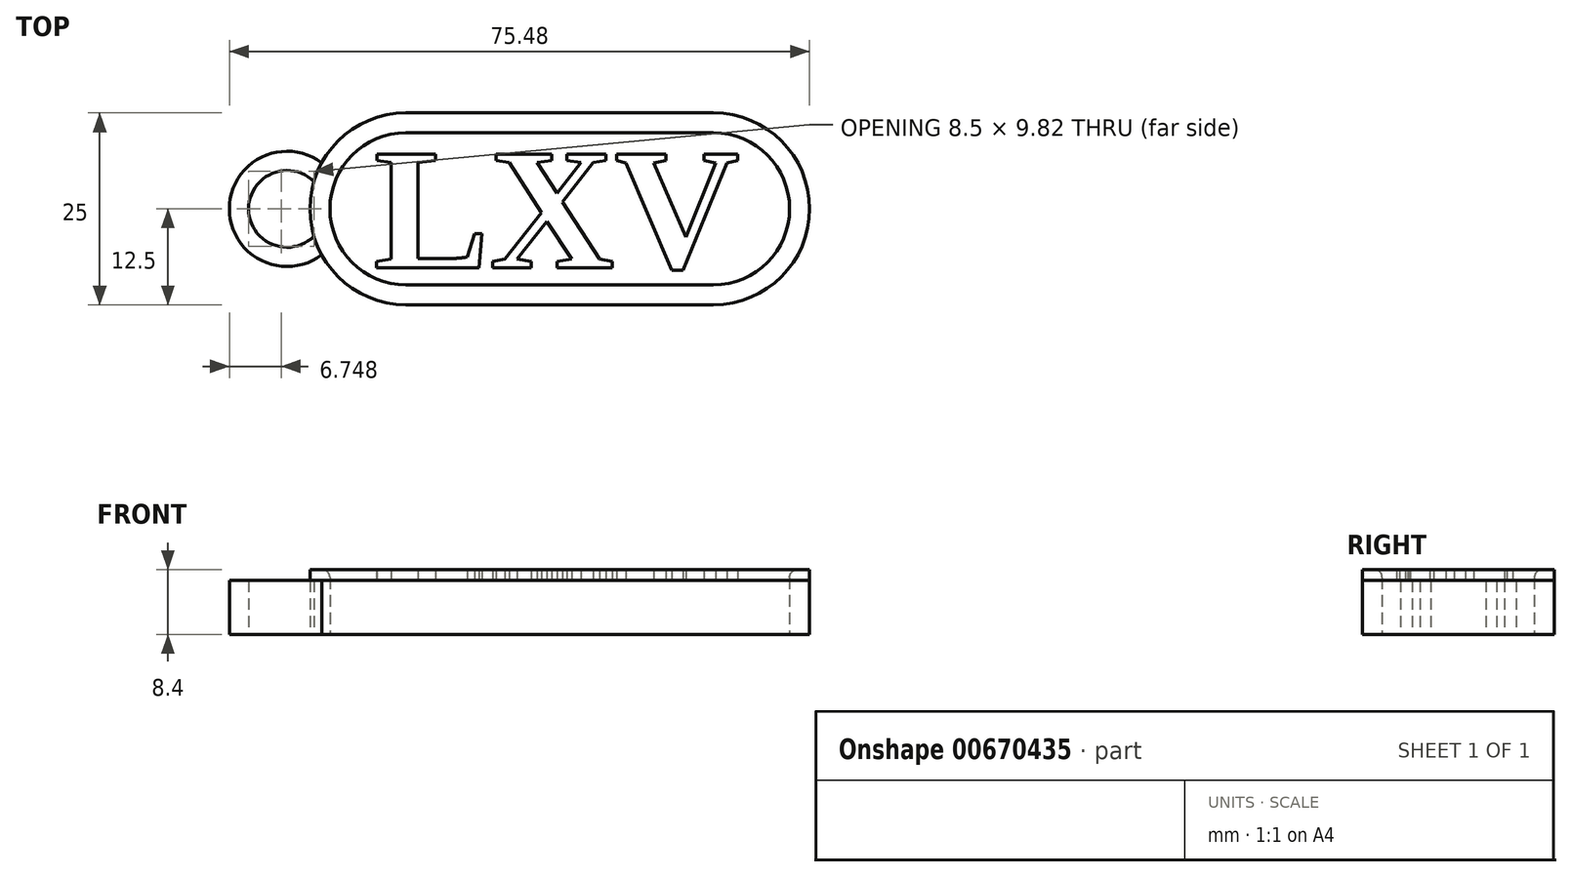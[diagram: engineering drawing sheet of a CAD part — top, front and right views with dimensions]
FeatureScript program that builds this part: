
annotation { "Feature Type Name" : "Feature", "Feature Type Description" : "" }
export const myFeature = defineFeature(function(context is Context, id is Id, definition is map)
    precondition{}
    {
        {
            var Q0;
            Q0=qCreatedBy(makeId("Top.planeOp"),FACE);
            var sketch = newSketch(context, id + "F0", { "sketchPlane" : qUnion([Q0])});
            skLineSegment(sketch, "E0.bottom", {"start": v(-20, 12.5) * mm, "end": v(20, 12.5) * mm});
            skLineSegment(sketch, "E0.top", {"start": v(-20, -12.5) * mm, "end": v(20, -12.5) * mm});
            skLineSegment(sketch, "E0.left", {"start": v(-20, 12.5) * mm, "end": v(-20, -12.5) * mm});
            skLineSegment(sketch, "E0.right", {"start": v(20, 12.5) * mm, "end": v(20, -12.5) * mm});
            skPoint(sketch, "E0.middle", {"position": v(0, 0) * mm});
            skArc(sketch, "E1", {"start": v(-20, 12.5) * mm, "mid": v(-32.5, 0) * mm, "end": v(-20, -12.5) * mm});
            skArc(sketch, "E2", {"start": v(20, 12.5) * mm, "mid": v(32.5, 0) * mm, "end": v(20, -12.5) * mm});
            skCircle(sketch, "E3", {"center": v(-35.48, 0) * mm, "radius": 5 * mm});
            skCircle(sketch, "E4", {"center": v(-35.48, 0) * mm, "radius": 7.5 * mm});
            skSolve(sketch);
        }
        {
            var Q0;
            {var subQ0=sQuery(id+"F0.wireOp",EDGE,"E0.left");Q0=makeQuery(id+"F0.imprint","IMPRINT",FACE,{"disambiguationData":[TD([[makeQuery(id+"F0.imprint","IMPRINT",EDGE,{"derivedFrom":subQ0}),-1.0]])]});}
            var Q1;
            Q1=makeQuery(id+"F0.imprint","IMPRINT",FACE,{"disambiguationData":[TD([[makeQuery(id+"F0.imprint","IMPRINT",EDGE,{"derivedFrom":sQuery(id+"F0.wireOp",EDGE,"E0.bottom")}),-1.0]])]});
            var Q2;
            Q2=makeQuery(id+"F0.imprint","IMPRINT",FACE,{"disambiguationData":[TD([[makeQuery(id+"F0.imprint","IMPRINT",EDGE,{"derivedFrom":sQuery(id+"F0.wireOp",EDGE,"E0.right")}),1.0]])]});
            var Q3;
            Q3=makeQuery(id+"F0.imprint","IMPRINT",FACE,{"disambiguationData":[TD([[makeQuery(id+"F0.imprint","IMPRINT",EDGE,{"derivedFrom":sQuery(id+"F0.wireOp",EDGE,"E4")}),-1.0]])]});
            var Q4;
            {var subQ0=sQuery(id+"F0.wireOp",EDGE,"E3");var subQ1=sQuery(id+"F0.wireOp",EDGE,"E1");var subQ2=makeQuery(id+"F0.imprint","INTERSECT",VERTEX,{"disambiguationData":[OD(0.0)],"derivedFrom":[subQ1,subQ0]});Q4=makeQuery(id+"F0.imprint","IMPRINT",FACE,{"disambiguationData":[TD([[makeQuery(id+"F0.imprint","IMPRINT",EDGE,{"disambiguationData":[TD([[subQ2,-1.0]])],"derivedFrom":subQ1}),1.0]])]});}
            extrude(context, id + "F1", {"entities" : qUnion([Q0, Q1, Q2, Q3, Q4]), "depth" : 5 * mm, "offsetDistance" : 25 * mm});
        }
        {
            var Q0;
            Q0=qCreatedBy(makeId("Top.planeOp"),FACE);
            var sketch = newSketch(context, id + "F2", { "sketchPlane" : qUnion([Q0])});
            skArc(sketch, "E5.0", {"start": v(-20, 9.9) * mm, "mid": v(-29.9, 0) * mm, "end": v(-20, -9.9) * mm});
            skLineSegment(sketch, "E5.1", {"start": v(-20, 9.9) * mm, "end": v(20, 9.9) * mm});
            skArc(sketch, "E5.2", {"start": v(20, 9.9) * mm, "mid": v(29.9, 0) * mm, "end": v(20, -9.9) * mm});
            skLineSegment(sketch, "E5.3", {"start": v(-20, -9.9) * mm, "end": v(20, -9.9) * mm});
            skLineSegment(sketch, "E6.0", {"start": v(-20, 12.5) * mm, "end": v(20, 12.5) * mm});
            skArc(sketch, "E6.1", {"start": v(-20, 12.5) * mm, "mid": v(-32.5, 0) * mm, "end": v(-20, -12.5) * mm});
            skLineSegment(sketch, "E6.2", {"start": v(-20, -12.5) * mm, "end": v(20, -12.5) * mm});
            skArc(sketch, "E6.3", {"start": v(20, 12.5) * mm, "mid": v(32.5, 0) * mm, "end": v(20, -12.5) * mm});
            skSolve(sketch);
        }
        {
            var Q0;
            Q0 = qSketchRegion(id + "F2", true);
            extrude(context, id + "F3", {"entities" : qUnion([Q0]), "operationType" : NewBodyOperationType.ADD, "depth" : 7 * mm, "offsetDistance" : 25 * mm});
        }
        {
            var Q0;
            {var subQ0=sQuery(id+"F0.wireOp",EDGE,"E4");var subQ1=sQuery(id+"F0.wireOp",EDGE,"E3");var subQ2=sQuery(id+"F0.wireOp",EDGE,"E1");var subQ4=sQuery(id+"F0.wireOp",EDGE,"E0.top");var subQ5=sQuery(id+"F0.wireOp",EDGE,"E0.bottom");Q0=makeQuery(id+"F3.boolean.opBoolean","SPLIT",FACE,{"disambiguationData":[TD([makeQuery(id+"F1.opExtrude","SWEPT_FACE",FACE,{"disambiguationData":[OSD([subQ1])]})])],"derivedFrom":makeQuery(id+"F1.opExtrude","CAP_FACE",FACE,{"disambiguationData":[OSD([subQ5,subQ4,subQ2,sQuery(id+"F0.wireOp",EDGE,"E2"),subQ1,subQ0])],"isStart":false})});}
            var Q1;
            Q1=makeQuery(id+"F3.opExtrude","CAP_FACE",FACE,{"disambiguationData":[OSD([sQuery(id+"F2.wireOp",EDGE,"E5.0"),sQuery(id+"F2.wireOp",EDGE,"E5.1"),sQuery(id+"F2.wireOp",EDGE,"E5.2"),sQuery(id+"F2.wireOp",EDGE,"E5.3"),sQuery(id+"F2.wireOp",EDGE,"E6.0"),sQuery(id+"F2.wireOp",EDGE,"E6.1"),sQuery(id+"F2.wireOp",EDGE,"E6.2"),sQuery(id+"F2.wireOp",EDGE,"E6.3")])],"isStart":false});
            extrude(context, id + "F4", {"entities" : qUnion([Q0]), "operationType" : NewBodyOperationType.ADD, "endBound" : BoundingType.UP_TO_SURFACE, "depth" : 25 * mm, "endBoundEntityFace" : qUnion([Q1]), "offsetDistance" : 25 * mm});
        }
        {
            var Q0;
            {var subQ0=sQuery(id+"F0.wireOp",EDGE,"E4");var subQ1=sQuery(id+"F0.wireOp",EDGE,"E1");var subQ2=makeQuery(id+"F0.imprint","INTERSECT",VERTEX,{"disambiguationData":[OD(0.0)],"derivedFrom":[subQ1,subQ0]});Q0=makeQuery(id+"F0.imprint","IMPRINT",FACE,{"disambiguationData":[TD([[makeQuery(id+"F0.imprint","IMPRINT",EDGE,{"disambiguationData":[TD([[subQ2,-1.0]])],"derivedFrom":subQ1}),-1.0]])]});}
            var Q1;
            {var subQ0=sQuery(id+"F0.wireOp",EDGE,"E4");var subQ1=sQuery(id+"F0.wireOp",EDGE,"E1");var subQ2=makeQuery(id+"F0.imprint","INTERSECT",VERTEX,{"disambiguationData":[OD(0.0)],"derivedFrom":[subQ1,subQ0]});Q1=makeQuery(id+"F0.imprint","IMPRINT",FACE,{"disambiguationData":[TD([[makeQuery(id+"F0.imprint","IMPRINT",EDGE,{"disambiguationData":[TD([[subQ2,-1.0]])],"derivedFrom":subQ1}),1.0]])]});}
            extrude(context, id + "F5", {"entities" : qUnion([Q0, Q1]), "operationType" : NewBodyOperationType.ADD, "depth" : 7 * mm, "offsetDistance" : 25 * mm});
        }
        {
            var Q0;
            Q0=qCreatedBy(makeId("Top.planeOp"),FACE);
            var sketch = newSketch(context, id + "F6", { "sketchPlane" : qUnion([Q0])});
            skText(sketch, "E7", { "text": "LXV", "fontName": "Tinos-Bold.ttf"});
            const initialGuessF6  = {"E7": [-0.0242, -0.00766, 1, 0, 0.01623]};
            skSetInitialGuess(sketch, initialGuessF6);
            skSolve(sketch);
        }
        {
            var Q0;
            Q0 = qSketchRegion(id + "F6", true);
            extrude(context, id + "F7", {"entities" : qUnion([Q0]), "operationType" : NewBodyOperationType.ADD, "depth" : 8.4 * mm, "offsetDistance" : 25 * mm});
        }
        {
            var Q0;
            Q0 = qSketchRegion(id + "F2", true);
            extrude(context, id + "F8", {"entities" : qUnion([Q0]), "depth" : 8.4 * mm, "offsetDistance" : 25 * mm});
        }
        {
            var Q0;
            Q0=makeQuery(id+"F8.opExtrude","CAP_EDGE",EDGE,{"disambiguationData":[OSD([sQuery(id+"F2.wireOp",EDGE,"E5.0")])],"isStart":false});
            fillet(context, id + "F9", {"entities" : qUnion([Q0]), "radius" : 1 * mm, "tangentPropagation" : true, "allowEdgeOverflow" : false});
        }
    });
